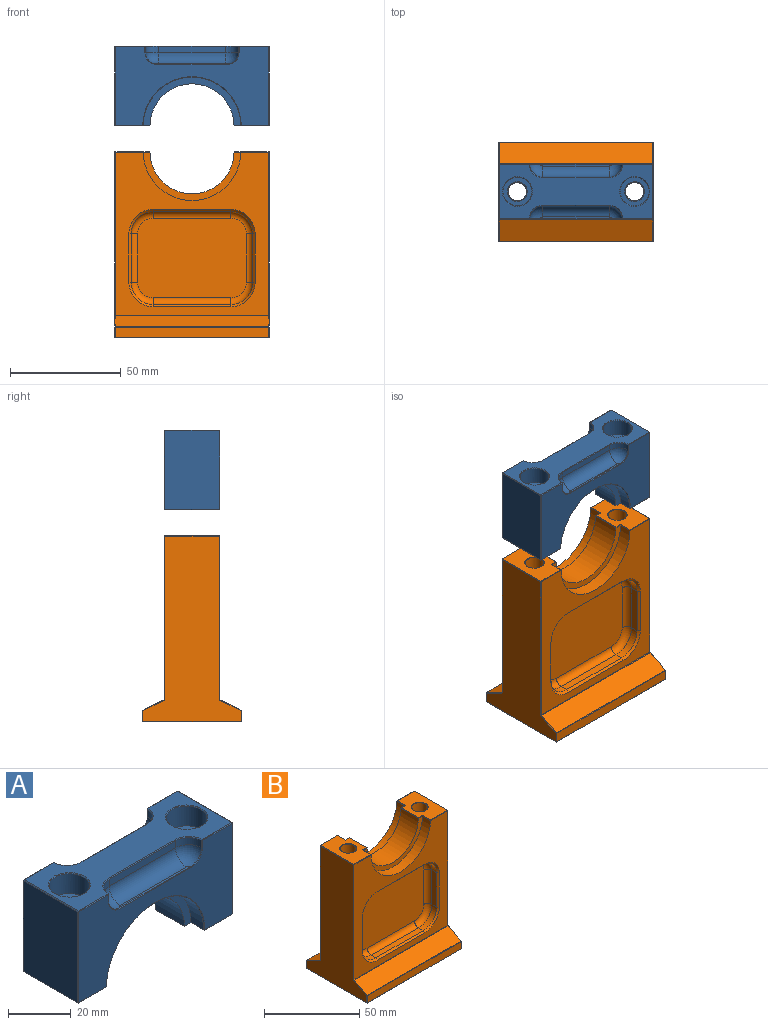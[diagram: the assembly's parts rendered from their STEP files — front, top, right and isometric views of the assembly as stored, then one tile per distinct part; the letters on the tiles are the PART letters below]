
ASSEMBLY  parts=2 mates=1
PART A: 98 faces, bbox 70x25x36 mm
  f0: plane 69.5x24.5mm, normal (0,0,1), area 940mm2, adj f37,f40,f46,f47,f48,f50,f54,f55
  f1: plane 69.52x35.52mm, normal (0,-1,0), area 1372.7mm2, adj f43,f44,f45,f51,f56,f57,f70,f71
  f2: cylinder r=22mm len=44mm, axis (0,1,0), area 394.6mm2, adj f11,f59,f66,f74,f85,f88
  f3: cylinder r=22mm len=44mm, axis (0,1,0), area 394.6mm2, adj f10,f79,f84,f90,f93,f94
  f4: plane 24.5x15.5mm, normal (0,0,-1), area 281.6mm2, adj f59,f61,f66,f72,f73,f79,f83,f84
  f5: plane 35.5x24.5mm, normal (1,0,0), area 869.8mm2, adj f58,f60,f71,f72
  f6: plane 35.5x24.5mm, normal (-1,0,0), area 869.8mm2, adj f68,f69,f81,f82
  f7: plane 24.5x15.5mm, normal (0,0,-1), area 281.6mm2, adj f34,f75,f81,f85,f88,f89,f91,f93
  f8: plane 69.52x35.52mm, normal (0,1,0), area 1372.7mm2, adj f35,f36,f38,f39,f42,f48,f54,f60
  f9: cylinder r=19mm len=38mm, axis (0,1,0), area 769.6mm2, adj f10,f11,f66,f73,f79,f88,f91,f93
  f10: plane 44x21.75mm, normal (0,-1,0), area 191.7mm2, adj f3,f9,f79,f93
  f11: plane 44x21.75mm, normal (0,1,0), area 191.7mm2, adj f2,f9,f66,f88
  f12: cylinder r=4.2mm len=27.5mm, axis (0,0,1), area 725.7mm2, adj f33,f34
  f13: cylinder r=4.2mm len=27.5mm, axis (0,0,1), area 725.7mm2, adj f32,f95
  f14: cylinder r=6.5mm len=13mm, axis (0,0,1), area 316.5mm2, adj f15,f96
  f15: plane 13x13mm, normal (0,0,1), area 70.5mm2, adj f14,f32
  f16: cylinder r=6.5mm len=13mm, axis (0,0,1), area 316.5mm2, adj f17,f97
  f17: plane 13x13mm, normal (0,0,1), area 70.5mm2, adj f16,f33
  f18: cylinder r=6mm len=6mm, axis (0,0,1), area 25.3mm2, adj f20,f29,f37,f38
  f19: cylinder r=6mm len=6mm, axis (0,0,1), area 25.3mm2, adj f20,f31,f42,f46
  f20: plane 30x2.75mm, normal (0,1,0), area 82.5mm2, adj f18,f19,f30,f40
  f21: plane 31.94x0.75mm, normal (0,0,1), area 23.6mm2, adj f29,f30,f31,f36
  f22: cylinder r=6mm len=6mm, axis (0,0,1), area 25.3mm2, adj f23,f26,f45,f47
  f23: plane 30x2.75mm, normal (0,-1,0), area 82.5mm2, adj f22,f24,f27,f50
  f24: cylinder r=6mm len=6mm, axis (0,0,1), area 25.3mm2, adj f23,f28,f55,f56
  f25: plane 31.94x0.76mm, normal (0,0,1), area 23.6mm2, adj f26,f27,f28,f44
  f26: torus R=1mm, axis (0,0,1), area 47.5mm2, adj f22,f25,f27,f43
  f27: cylinder r=5mm len=30mm, axis (-1,0,0), area 235.6mm2, adj f23,f25,f26,f28
  f28: torus R=1mm, axis (0,0,1), area 47.5mm2, adj f24,f25,f27,f51
  f29: torus R=1mm, axis (0,0,1), area 47.5mm2, adj f18,f21,f30,f35
  f30: cylinder r=5mm len=30mm, axis (1,0,0), area 235.6mm2, adj f20,f21,f29,f31
  f31: torus R=1mm, axis (0,0,1), area 47.5mm2, adj f19,f21,f30,f39
  f32: cone r=4.45mm half-angle=45deg, axis (0,0,1), area 9.6mm2, adj f13,f15
  f33: cone r=4.2mm half-angle=45deg, axis (0,0,1), area 9.6mm2, adj f12,f17
  f34: cone r=4.2mm half-angle=45deg, axis (0,0,-1), area 9.6mm2, adj f7,f12
  f35: bspline ~5.28x5.26mm, area 2.8mm2, adj f8,f29,f36,f38
  f36: plane 31.94x0.25mm, normal (0,0.71,0.71), area 11.3mm2, adj f8,f21,f35,f39
  f37: cone r=6.25mm half-angle=45deg, axis (0,0,1), area 3.3mm2, adj f0,f18,f40,f41
  f38: plane 2.75x0.25mm, normal (-0.69,0.72,0), area 1mm2, adj f8,f18,f35,f41
  f39: bspline ~5.28x5.26mm, area 2.8mm2, adj f8,f31,f36,f42
  f40: plane 30x0.25mm, normal (0,0.71,0.71), area 10.6mm2, adj f0,f20,f37,f46
  f41: plane 0.25x0.25mm, normal (-0.56,0.58,0.58), area 0.1mm2, adj f37,f38,f48
  f42: plane 2.75x0.25mm, normal (0.69,0.72,0), area 1mm2, adj f8,f19,f39,f49
  f43: bspline ~5.28x5.26mm, area 2.8mm2, adj f1,f26,f44,f45
  f44: plane 31.94x0.25mm, normal (0,-0.71,0.71), area 11.1mm2, adj f1,f25,f43,f51
  f45: plane 2.75x0.25mm, normal (-0.69,-0.72,0), area 1mm2, adj f1,f22,f43,f52
  f46: cone r=6.25mm half-angle=45deg, axis (0,0,1), area 3.3mm2, adj f0,f19,f40,f49
  f47: cone r=6mm half-angle=45deg, axis (0,0,1), area 3.3mm2, adj f0,f22,f50,f52
  f48: plane 13.51x0.25mm, normal (0,0.71,0.71), area 4.8mm2, adj f0,f8,f41,f53
  f49: plane 0.25x0.25mm, normal (0.56,0.58,0.58), area 0.1mm2, adj f42,f46,f54
  f50: plane 30x0.25mm, normal (0,-0.71,0.71), area 10.6mm2, adj f0,f23,f47,f55
  f51: bspline ~5.28x5.26mm, area 2.8mm2, adj f1,f28,f44,f56
  f52: plane 0.25x0.25mm, normal (-0.56,-0.58,0.58), area 0.1mm2, adj f45,f47,f57
  f53: plane 0.25x0.25mm, normal (0.58,0.58,0.58), area 0.1mm2, adj f48,f58,f60
  f54: plane 13.51x0.25mm, normal (0,0.71,0.71), area 4.8mm2, adj f0,f8,f49,f62
  f55: cone r=6mm half-angle=45deg, axis (0,0,1), area 3.3mm2, adj f0,f24,f50,f63
  f56: plane 2.75x0.25mm, normal (0.69,-0.72,0), area 1mm2, adj f1,f24,f51,f63
  f57: plane 13.51x0.25mm, normal (0,-0.71,0.71), area 4.8mm2, adj f0,f1,f52,f64
  f58: plane 24.5x0.25mm, normal (0.71,0,0.71), area 8.7mm2, adj f0,f5,f53,f64
  f59: plane 6x0.25mm, normal (-0.7,0,-0.71), area 2.1mm2, adj f2,f4,f66,f67
  f60: plane 35.5x0.25mm, normal (0.71,0.71,0), area 12.6mm2, adj f5,f8,f53,f65
  f61: plane 12.5x0.25mm, normal (0,0.71,-0.71), area 4.4mm2, adj f4,f8,f65,f67
  f62: plane 0.25x0.25mm, normal (-0.58,0.58,0.58), area 0.1mm2, adj f54,f68,f69
  f63: plane 0.25x0.25mm, normal (0.56,-0.58,0.58), area 0.1mm2, adj f55,f56,f70
  f64: plane 0.25x0.25mm, normal (0.58,-0.58,0.58), area 0.1mm2, adj f57,f58,f71
  f65: plane 0.25x0.25mm, normal (0.58,0.58,-0.58), area 0.1mm2, adj f60,f61,f72
  f66: plane 3.25x0.25mm, normal (0,0.71,-0.71), area 1.1mm2, adj f2,f4,f9,f11,f59,f73
  f67: plane 0.25x0.25mm, normal (-0.57,0.58,-0.58), area 0.1mm2, adj f59,f61,f74
  f68: plane 35.5x0.25mm, normal (-0.71,0.71,0), area 12.6mm2, adj f6,f8,f62,f76
  f69: plane 24.5x0.25mm, normal (-0.71,0,0.71), area 8.7mm2, adj f0,f6,f62,f77
  f70: plane 13.51x0.25mm, normal (0,-0.71,0.71), area 4.8mm2, adj f0,f1,f63,f77
  f71: plane 35.5x0.25mm, normal (0.71,-0.71,0), area 12.6mm2, adj f1,f5,f64,f78
  f72: plane 24.5x0.25mm, normal (0.71,0,-0.71), area 8.7mm2, adj f4,f5,f65,f78
  f73: plane 12.99x0.25mm, normal (-0.7,0,-0.71), area 4.5mm2, adj f4,f9,f66,f79
  f74: cone r=22.25mm half-angle=45deg, axis (0,1,0), area 24.4mm2, adj f2,f8,f67,f80
  f75: plane 12.5x0.25mm, normal (0,0.71,-0.71), area 4.4mm2, adj f7,f8,f76,f80
  f76: plane 0.25x0.25mm, normal (-0.58,0.58,-0.58), area 0.1mm2, adj f68,f75,f81
  f77: plane 0.25x0.25mm, normal (-0.58,-0.58,0.58), area 0.1mm2, adj f69,f70,f82
  f78: plane 0.25x0.25mm, normal (0.58,-0.58,-0.58), area 0.1mm2, adj f71,f72,f83
  f79: plane 3.25x0.25mm, normal (0,-0.71,-0.71), area 1.1mm2, adj f3,f4,f9,f10,f73,f84
  f80: plane 0.25x0.25mm, normal (0.57,0.58,-0.58), area 0.1mm2, adj f74,f75,f85
  f81: plane 24.5x0.25mm, normal (-0.71,0,-0.71), area 8.7mm2, adj f6,f7,f76,f86
  f82: plane 35.5x0.25mm, normal (-0.71,-0.71,0), area 12.6mm2, adj f1,f6,f77,f86
  f83: plane 12.5x0.25mm, normal (0,-0.71,-0.71), area 4.4mm2, adj f1,f4,f78,f87
  f84: plane 6x0.25mm, normal (-0.7,0,-0.71), area 2.1mm2, adj f3,f4,f79,f87
  f85: plane 6x0.25mm, normal (0.7,0,-0.71), area 2.1mm2, adj f2,f7,f80,f88
  f86: plane 0.25x0.25mm, normal (-0.58,-0.58,-0.58), area 0.1mm2, adj f81,f82,f89
  f87: plane 0.25x0.25mm, normal (-0.57,-0.58,-0.58), area 0.1mm2, adj f83,f84,f90
  f88: plane 3.25x0.25mm, normal (0,0.71,-0.71), area 1.1mm2, adj f2,f7,f9,f11,f85,f91
  f89: plane 12.5x0.25mm, normal (0,-0.71,-0.71), area 4.4mm2, adj f1,f7,f86,f92
  f90: cone r=22mm half-angle=45deg, axis (0,-1,0), area 24.4mm2, adj f1,f3,f87,f92
  f91: plane 12.99x0.25mm, normal (0.7,0,-0.71), area 4.5mm2, adj f7,f9,f88,f93
  f92: plane 0.25x0.25mm, normal (0.57,-0.58,-0.58), area 0.1mm2, adj f89,f90,f94
  f93: plane 3.25x0.25mm, normal (0,-0.71,-0.71), area 1.1mm2, adj f3,f7,f9,f10,f91,f94
  f94: plane 6x0.25mm, normal (0.7,0,-0.71), area 2.1mm2, adj f3,f7,f92,f93
  f95: cone r=4.45mm half-angle=45deg, axis (0,0,-1), area 9.6mm2, adj f4,f13
  f96: cone r=6.75mm half-angle=45deg, axis (0,0,1), area 14.7mm2, adj f0,f14
  f97: cone r=6.5mm half-angle=45deg, axis (0,0,1), area 14.7mm2, adj f0,f16
PART B: 122 faces, bbox 70x45x84 mm
  f0: plane 73.65x69.5mm, normal (0,1,0), area 1962.8mm2, adj f3,f20,f29,f39,f44,f48,f106,f107
  f1: plane 73.65x69.5mm, normal (0,-1,0), area 1962.8mm2, adj f4,f24,f33,f53,f57,f58,f114,f115
  f2: plane 69.5x44.5mm, normal (0,0,-1), area 2968.3mm2, adj f46,f54,f55,f56,f70,f71
  f3: cylinder r=22mm len=44mm, axis (0,1,0), area 412.3mm2, adj f0,f11,f19,f20,f21,f28,f29,f30
  f4: cylinder r=22mm len=44mm, axis (0,1,0), area 412.3mm2, adj f1,f10,f24,f25,f26,f33,f34,f35
  f5: plane 24.6x15.6mm, normal (0,0,1), area 287mm2, adj f18,f19,f20,f21,f22,f23,f24,f25
  f6: plane 83.45x44.5mm, normal (-1,0,0), area 2186.4mm2, adj f38,f43,f47,f48,f52,f56,f57,f62
  f7: plane 83.45x44.5mm, normal (1,0,0), area 2186.4mm2, adj f36,f40,f44,f45,f49,f53,f54,f59
  f8: plane 24.6x15.6mm, normal (0,0,1), area 287mm2, adj f27,f28,f29,f30,f31,f32,f33,f34
  f9: cylinder r=19mm len=38mm, axis (0,1,0), area 770.8mm2, adj f10,f11,f21,f23,f25,f30,f32,f34
  f10: plane 44x21.8mm, normal (0,-1,0), area 192mm2, adj f4,f9,f25,f34
  f11: plane 44x21.8mm, normal (0,1,0), area 192mm2, adj f3,f9,f21,f30
  f12: plane 69.5x4.6mm, normal (0,-1,0), area 319.4mm2, adj f55,f64,f65,f69
  f13: plane 69.5x4.6mm, normal (0,1,0), area 319.4mm2, adj f37,f45,f46,f47
  f14: plane 69.5x9.72mm, normal (0,-0.45,0.89), area 755.6mm2, adj f58,f63,f66,f69
  f15: plane 69.5x9.72mm, normal (0,0.45,0.89), area 755.6mm2, adj f36,f37,f38,f39
  f16: cylinder r=4.2mm len=83.55mm, axis (0,0,1), area 2204.8mm2, adj f18,f70
  f17: cylinder r=4.2mm len=83.55mm, axis (0,0,1), area 2204.8mm2, adj f27,f71
  f18: cone r=4.4mm half-angle=45deg, axis (0,0,1), area 7.6mm2, adj f5,f16
  f19: plane 6.2x0.2mm, normal (0.7,0,0.71), area 1.7mm2, adj f3,f5,f20,f21
  f20: plane 12.88x0.2mm, normal (0,0.71,0.71), area 3.6mm2, adj f0,f3,f5,f19,f22,f48
  f21: plane 3.2x0.2mm, normal (0,0.71,0.71), area 0.8mm2, adj f3,f5,f9,f11,f19,f23
  f22: plane 24.75x0.13mm, normal (-0.71,0,0.71), area 4.4mm2, adj f5,f20,f24,f48,f52,f57
  f23: plane 13x0.2mm, normal (0.7,0,0.71), area 3.6mm2, adj f5,f9,f21,f25
  f24: plane 12.88x0.2mm, normal (0,-0.71,0.71), area 3.6mm2, adj f1,f4,f5,f22,f26,f57
  f25: plane 3.2x0.2mm, normal (0,-0.71,0.71), area 0.8mm2, adj f4,f5,f9,f10,f23,f26
  f26: plane 6.2x0.2mm, normal (0.7,0,0.71), area 1.7mm2, adj f4,f5,f24,f25
  f27: cone r=4.2mm half-angle=45deg, axis (0,0,1), area 7.6mm2, adj f8,f17
  f28: plane 6.2x0.2mm, normal (-0.7,0,0.71), area 1.7mm2, adj f3,f8,f29,f30
  f29: plane 12.88x0.2mm, normal (0,0.71,0.71), area 3.6mm2, adj f0,f3,f8,f28,f31,f44
  f30: plane 3.2x0.2mm, normal (0,0.71,0.71), area 0.8mm2, adj f3,f8,f9,f11,f28,f32
  f31: plane 24.75x0.13mm, normal (0.71,0,0.71), area 4.4mm2, adj f8,f29,f33,f44,f49,f53
  f32: plane 13x0.2mm, normal (-0.7,0,0.71), area 3.6mm2, adj f8,f9,f30,f34
  f33: plane 12.88x0.2mm, normal (0,-0.71,0.71), area 3.6mm2, adj f1,f4,f8,f31,f35,f53
  f34: plane 3.2x0.2mm, normal (0,-0.71,0.71), area 0.8mm2, adj f4,f8,f9,f10,f32,f35
  f35: plane 6.2x0.2mm, normal (-0.7,0,0.71), area 1.7mm2, adj f4,f8,f33,f34
  f36: plane 9.84x5.09mm, normal (0.71,0.32,0.63), area 3.8mm2, adj f7,f15,f40,f41
  f37: plane 69.5x0.22mm, normal (0,0.85,0.53), area 18.3mm2, adj f13,f15,f41,f42
  f38: plane 9.84x5.09mm, normal (-0.71,0.32,0.63), area 3.8mm2, adj f6,f15,f42,f43
  f39: plane 69.5x0.22mm, normal (0,0.85,0.53), area 18.3mm2, adj f0,f15,f40,f43
  f40: plane 0.45x0.39mm, normal (0.65,0.65,0.4), area 0.1mm2, adj f7,f36,f39,f44
  f41: plane 0.25x0.25mm, normal (0.65,0.65,0.4), area 0mm2, adj f36,f37,f45
  f42: plane 0.25x0.25mm, normal (-0.65,0.65,0.4), area 0mm2, adj f37,f38,f47
  f43: plane 0.45x0.39mm, normal (-0.65,0.65,0.4), area 0.1mm2, adj f6,f38,f39,f48
  f44: plane 73.77x0.25mm, normal (0.71,0.71,0), area 26.1mm2, adj f0,f7,f29,f31,f40,f49
  f45: plane 4.6x0.25mm, normal (0.71,0.71,0), area 1.6mm2, adj f7,f13,f41,f50
  f46: plane 69.5x0.25mm, normal (0,0.71,-0.71), area 24.6mm2, adj f2,f13,f50,f51
  f47: plane 4.6x0.25mm, normal (-0.71,0.71,0), area 1.6mm2, adj f6,f13,f42,f51
  f48: plane 73.77x0.25mm, normal (-0.71,0.71,0), area 26.1mm2, adj f0,f6,f20,f22,f43,f52
  f49: plane 24.65x0.18mm, normal (0.92,0,0.38), area 4.7mm2, adj f7,f31,f44,f53
  f50: plane 0.25x0.25mm, normal (0.58,0.58,-0.58), area 0.1mm2, adj f45,f46,f54
  f51: plane 0.25x0.25mm, normal (-0.58,0.58,-0.58), area 0.1mm2, adj f46,f47,f56
  f52: plane 24.65x0.18mm, normal (-0.92,0,0.38), area 4.7mm2, adj f6,f22,f48,f57
  f53: plane 73.77x0.25mm, normal (0.71,-0.71,0), area 26.1mm2, adj f1,f7,f31,f33,f49,f59
  f54: plane 44.5x0.25mm, normal (0.71,0,-0.71), area 15.7mm2, adj f2,f7,f50,f60
  f55: plane 69.5x0.25mm, normal (0,-0.71,-0.71), area 24.6mm2, adj f2,f12,f60,f61
  f56: plane 44.5x0.25mm, normal (-0.71,0,-0.71), area 15.7mm2, adj f2,f6,f51,f61
  f57: plane 73.77x0.25mm, normal (-0.71,-0.71,0), area 26.1mm2, adj f1,f6,f22,f24,f52,f62
  f58: plane 69.5x0.22mm, normal (0,-0.85,0.53), area 18.3mm2, adj f1,f14,f59,f62
  f59: plane 0.45x0.39mm, normal (0.65,-0.65,0.4), area 0.1mm2, adj f7,f53,f58,f63
  f60: plane 0.25x0.25mm, normal (0.58,-0.58,-0.58), area 0.1mm2, adj f54,f55,f64
  f61: plane 0.25x0.25mm, normal (-0.58,-0.58,-0.58), area 0.1mm2, adj f55,f56,f65
  f62: plane 0.45x0.39mm, normal (-0.65,-0.65,0.4), area 0.1mm2, adj f6,f57,f58,f66
  f63: plane 9.84x5.09mm, normal (0.71,-0.32,0.63), area 3.8mm2, adj f7,f14,f59,f67
  f64: plane 4.6x0.25mm, normal (0.71,-0.71,0), area 1.6mm2, adj f7,f12,f60,f67
  f65: plane 4.6x0.25mm, normal (-0.71,-0.71,0), area 1.6mm2, adj f6,f12,f61,f68
  f66: plane 9.84x5.09mm, normal (-0.71,-0.32,0.63), area 3.8mm2, adj f6,f14,f62,f68
  f67: plane 0.25x0.25mm, normal (0.65,-0.65,0.4), area 0mm2, adj f63,f64,f69
  f68: plane 0.25x0.25mm, normal (-0.65,-0.65,0.4), area 0mm2, adj f65,f66,f69
  f69: plane 69.5x0.22mm, normal (0,-0.85,0.53), area 18.3mm2, adj f12,f14,f67,f68
  f70: cone r=4.45mm half-angle=45deg, axis (0,0,-1), area 9.6mm2, adj f2,f16
  f71: cone r=4.2mm half-angle=45deg, axis (0,0,-1), area 9.6mm2, adj f2,f17
  f72: plane 35x3.5mm, normal (0,0,1), area 122.5mm2, adj f73,f79,f102,f117
  f73: cylinder r=10mm len=10mm, axis (0,1,0), area 55mm2, adj f72,f74,f104,f119
  f74: plane 22x3.5mm, normal (-1,0,0), area 77mm2, adj f73,f75,f105,f121
  f75: cylinder r=10mm len=10mm, axis (0,1,0), area 55mm2, adj f74,f76,f103,f120
  f76: plane 35x3.5mm, normal (0,0,-1), area 122.5mm2, adj f75,f77,f101,f118
  f77: cylinder r=10mm len=10mm, axis (0,1,0), area 55mm2, adj f76,f78,f99,f116
  f78: plane 22x3.5mm, normal (1,0,0), area 77mm2, adj f77,f79,f98,f114
  f79: cylinder r=10mm len=10mm, axis (0,1,0), area 55mm2, adj f72,f78,f100,f115
  f80: plane 49x36mm, normal (0,-1,0), area 1721.9mm2, adj f98,f99,f100,f101,f102,f103,f104,f105
  f81: plane 35x3.5mm, normal (0,0,1), area 122.5mm2, adj f82,f88,f94,f110
  f82: cylinder r=10mm len=10mm, axis (0,-1,0), area 55mm2, adj f81,f83,f96,f112
  f83: plane 22x3.5mm, normal (-1,0,0), area 77mm2, adj f82,f84,f97,f113
  f84: cylinder r=10mm len=10mm, axis (0,-1,0), area 55mm2, adj f83,f85,f95,f111
  f85: plane 35x3.5mm, normal (0,0,-1), area 122.5mm2, adj f84,f86,f93,f109
  f86: cylinder r=10mm len=10mm, axis (0,-1,0), area 55mm2, adj f85,f87,f91,f107
  f87: plane 22x3.5mm, normal (1,0,0), area 77mm2, adj f86,f88,f90,f106
  f88: cylinder r=10mm len=10mm, axis (0,-1,0), area 55mm2, adj f81,f87,f92,f108
  f89: plane 49x36mm, normal (0,1,0), area 1721.9mm2, adj f90,f91,f92,f93,f94,f95,f96,f97
  f90: cylinder r=3mm len=22mm, axis (0,0,1), area 103.7mm2, adj f87,f89,f91,f92
  f91: torus R=7mm, axis (0,-1,0), area 66mm2, adj f86,f89,f90,f93
  f92: torus R=7mm, axis (0,-1,0), area 66mm2, adj f88,f89,f90,f94
  f93: cylinder r=3mm len=35mm, axis (1,0,0), area 164.9mm2, adj f85,f89,f91,f95
  f94: cylinder r=3mm len=35mm, axis (-1,0,0), area 164.9mm2, adj f81,f89,f92,f96
  f95: torus R=7mm, axis (0,-1,0), area 66mm2, adj f84,f89,f93,f97
  f96: torus R=7mm, axis (0,-1,0), area 66mm2, adj f82,f89,f94,f97
  f97: cylinder r=3mm len=22mm, axis (0,0,-1), area 103.7mm2, adj f83,f89,f95,f96
  f98: cylinder r=3mm len=22mm, axis (0,0,1), area 103.7mm2, adj f78,f80,f99,f100
  f99: torus R=7mm, axis (0,-1,0), area 66mm2, adj f77,f80,f98,f101
  f100: torus R=7mm, axis (0,-1,0), area 66mm2, adj f79,f80,f98,f102
  f101: cylinder r=3mm len=35mm, axis (1,0,0), area 164.9mm2, adj f76,f80,f99,f103
  f102: cylinder r=3mm len=35mm, axis (-1,0,0), area 164.9mm2, adj f72,f80,f100,f104
  f103: torus R=7mm, axis (0,-1,0), area 66mm2, adj f75,f80,f101,f105
  f104: torus R=7mm, axis (0,-1,0), area 66mm2, adj f73,f80,f102,f105
  f105: cylinder r=3mm len=22mm, axis (0,0,-1), area 103.7mm2, adj f74,f80,f103,f104
  f106: plane 22x1mm, normal (0.71,0.71,0), area 31.1mm2, adj f0,f87,f107,f108
  f107: cone r=11mm half-angle=45deg, axis (0,1,0), area 23.3mm2, adj f0,f86,f106,f109
  f108: cone r=11mm half-angle=45deg, axis (0,1,0), area 23.3mm2, adj f0,f88,f106,f110
  f109: plane 35x1mm, normal (0,0.71,-0.71), area 49.5mm2, adj f0,f85,f107,f111
  f110: plane 35x1mm, normal (0,0.71,0.71), area 49.5mm2, adj f0,f81,f108,f112
  f111: cone r=11mm half-angle=45deg, axis (0,1,0), area 23.3mm2, adj f0,f84,f109,f113
  f112: cone r=11mm half-angle=45deg, axis (0,1,0), area 23.3mm2, adj f0,f82,f110,f113
  f113: plane 22x1mm, normal (-0.71,0.71,0), area 31.1mm2, adj f0,f83,f111,f112
  f114: plane 22x1mm, normal (0.71,-0.71,0), area 31.1mm2, adj f1,f78,f115,f116
  f115: cone r=11mm half-angle=45deg, axis (0,-1,0), area 23.3mm2, adj f1,f79,f114,f117
  f116: cone r=11mm half-angle=45deg, axis (0,-1,0), area 23.3mm2, adj f1,f77,f114,f118
  f117: plane 35x1mm, normal (0,-0.71,0.71), area 49.5mm2, adj f1,f72,f115,f119
  f118: plane 35x1mm, normal (0,-0.71,-0.71), area 49.5mm2, adj f1,f76,f116,f120
  f119: cone r=11mm half-angle=45deg, axis (0,-1,0), area 23.3mm2, adj f1,f73,f117,f121
  f120: cone r=11mm half-angle=45deg, axis (0,-1,0), area 23.3mm2, adj f1,f75,f118,f121
  f121: plane 22x1mm, normal (-0.71,-0.71,0), area 31.1mm2, adj f1,f74,f119,f120
PLACE A t=(60.56,50.38,15.95)mm
PLACE B t=(60.56,50.38,-50.71)mm
MATE slider A.f13 <-> B.f17  axis (0,0,-1) through (87.06,50.38,-2.05)mm
